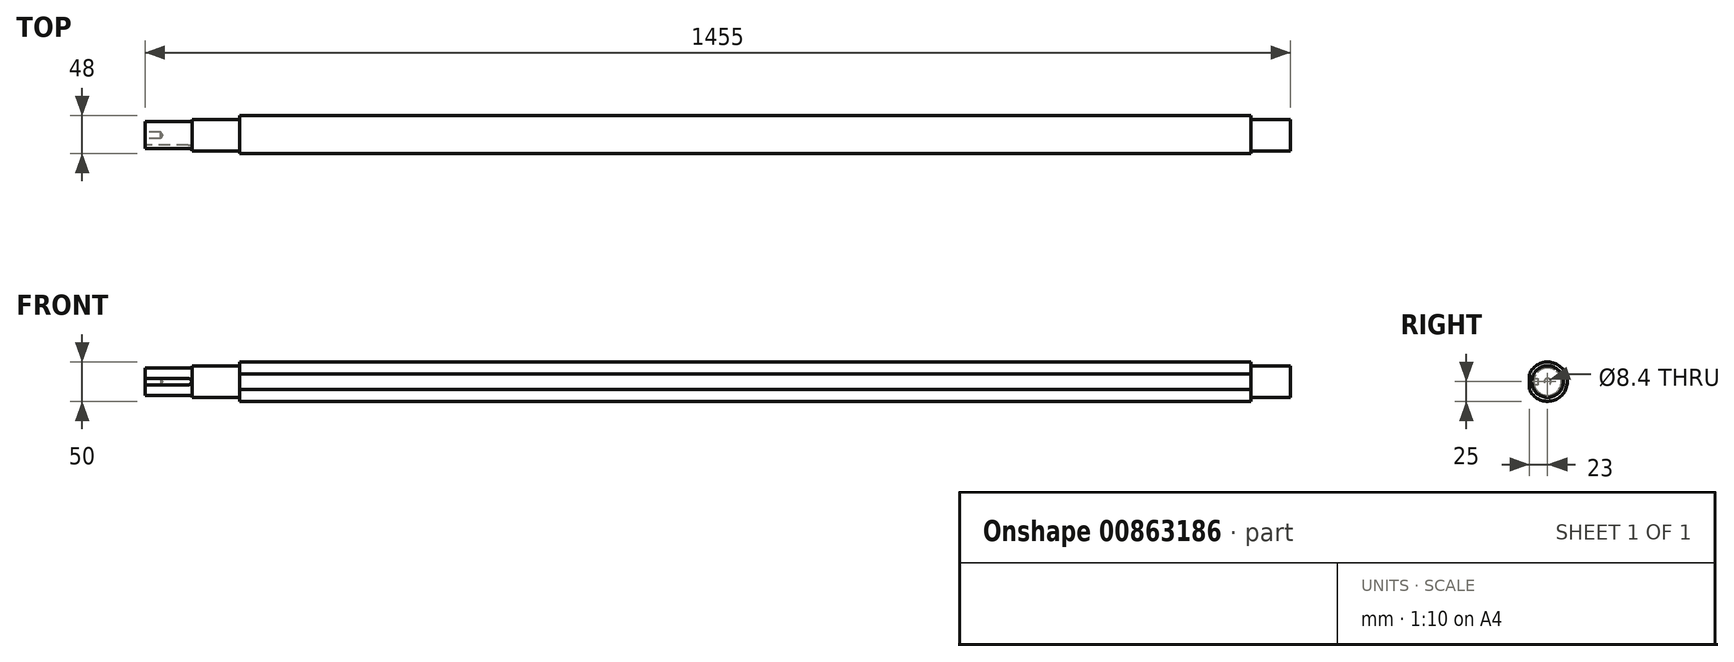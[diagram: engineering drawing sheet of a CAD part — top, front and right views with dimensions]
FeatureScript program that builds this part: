
annotation { "Feature Type Name" : "Feature", "Feature Type Description" : "" }
export const myFeature = defineFeature(function(context is Context, id is Id, definition is map)
    precondition{}
    {
        {
            var Q0;
            Q0=qCreatedBy(makeId("Front.planeOp"),FACE);
            var sketch = newSketch(context, id + "F0", { "sketchPlane" : qUnion([Q0])});
            skLineSegment(sketch, "E0", {"start": v(-727.5, 0) * mm, "end": v(727.5, 0) * mm});
            skLineSegment(sketch, "E1", {"start": v(727.5, 0) * mm, "end": v(727.5, -20) * mm});
            skLineSegment(sketch, "E2", {"start": v(727.5, -20) * mm, "end": v(677.5, -20) * mm});
            skLineSegment(sketch, "E3", {"start": v(677.5, -20) * mm, "end": v(677.5, -25) * mm});
            skLineSegment(sketch, "E4", {"start": v(677.5, -25) * mm, "end": v(-607.5, -25) * mm});
            skLineSegment(sketch, "E5", {"start": v(-607.5, -25) * mm, "end": v(-607.5, -20) * mm});
            skLineSegment(sketch, "E6", {"start": v(-607.5, -20) * mm, "end": v(-667.5, -20) * mm});
            skLineSegment(sketch, "E7", {"start": v(-727.5, -17.5) * mm, "end": v(-727.5, 0) * mm});
            skLineSegment(sketch, "E8", {"start": v(-727.5, -17.5) * mm, "end": v(-667.5, -17.5) * mm});
            skLineSegment(sketch, "E9", {"start": v(-667.5, -17.5) * mm, "end": v(-667.5, -20) * mm});
            skSolve(sketch);
        }
        {
            var Q0;
            Q0=makeQuery(id+"F0.imprint","IMPRINT",FACE,{"disambiguationData":[TD([[makeQuery(id+"F0.imprint","IMPRINT",EDGE,{"derivedFrom":sQuery(id+"F0.wireOp",EDGE,"E0")}),-1.0]])]});
            var Q1;
            Q1=sQuery(id+"F0.wireOp",EDGE,"E0");
            revolve(context, id + "F1", {"surfaceOperationType" : NewSurfaceOperationType.NEW, "entities" : qUnion([Q0]), "axis" : qUnion([Q1]), "revolveType" : RevolveType.FULL});
        }
        {
            var Q0;
            Q0=makeQuery(id+"F1.opRevolve","SWEPT_FACE",FACE,{"disambiguationData":[OSD([sQuery(id+"F0.wireOp",EDGE,"E7")])]});
            var sketch = newSketch(context, id + "F2", { "sketchPlane" : qUnion([Q0])});
            skLineSegment(sketch, "E10", {"start": v(12.5, 4) * mm, "end": v(12.5, -4) * mm});
            skLineSegment(sketch, "E11", {"start": v(12.5, -4) * mm, "end": v(17.5, -4) * mm});
            skLineSegment(sketch, "E12", {"start": v(17.5, -4) * mm, "end": v(17.5, 4) * mm});
            skLineSegment(sketch, "E13", {"start": v(17.5, 4) * mm, "end": v(12.5, 4) * mm});
            skSolve(sketch);
        }
        {
            var Q0;
            Q0=qSketchRegion(id+"F2",true);
            extrude(context, id + "F3", {"entities" : qUnion([Q0]), "operationType" : NewBodyOperationType.REMOVE, "oppositeDirection" : true, "depth" : 59 * mm, "offsetDistance" : 25 * mm});
        }
        {
            var Q0;
            Q0=makeQuery(id+"F1.opRevolve","SWEPT_FACE",FACE,{"disambiguationData":[OSD([sQuery(id+"F0.wireOp",EDGE,"E5")])]});
            var sketch = newSketch(context, id + "F4", { "sketchPlane" : qUnion([Q0])});
            skLineSegment(sketch, "E14.bottom", {"start": v(34.9, 15.3) * mm, "end": v(23, 15.3) * mm});
            skLineSegment(sketch, "E14.top", {"start": v(34.9, -18.86) * mm, "end": v(23, -18.86) * mm});
            skLineSegment(sketch, "E14.left", {"start": v(34.9, 15.3) * mm, "end": v(34.9, -18.86) * mm});
            skLineSegment(sketch, "E14.right", {"start": v(23, 15.3) * mm, "end": v(23, -18.86) * mm});
            skSolve(sketch);
        }
        {
            var Q0;
            Q0 = qSketchRegion(id + "F4", true);
            var Q1;
            Q1=makeQuery(id+"F1.opRevolve","SWEPT_FACE",FACE,{"disambiguationData":[OSD([sQuery(id+"F0.wireOp",EDGE,"E3")])]});
            extrude(context, id + "F5", {"entities" : qUnion([Q0, Q1]), "operationType" : NewBodyOperationType.REMOVE, "endBound" : BoundingType.THROUGH_ALL, "oppositeDirection" : true, "depth" : 25 * mm, "offsetDistance" : 25 * mm});
        }
        {
            var Q0;
            Q0=makeQuery(id+"F3.boolean.opBoolean","COPY",EDGE,{"derivedFrom":makeQuery(id+"F3.opExtrude","CAP_EDGE",EDGE,{"disambiguationData":[OSD([sQuery(id+"F2.wireOp",EDGE,"E13")])],"isStart":false})});
            var Q1;
            Q1=makeQuery(id+"F3.boolean.opBoolean","COPY",EDGE,{"derivedFrom":makeQuery(id+"F3.opExtrude","CAP_EDGE",EDGE,{"disambiguationData":[OSD([sQuery(id+"F2.wireOp",EDGE,"E11")])],"isStart":false})});
            fillet(context, id + "F6", {"entities" : qUnion([Q0, Q1]), "tangentPropagation" : true, "radius" : 4 * mm, "defaultsChanged" : false, "vertexSettings" : [], "allowEdgeOverflow" : false});
        }
        {
            var Q0;
            Q0=makeQuery(id+"F1.opRevolve","SWEPT_FACE",FACE,{"disambiguationData":[OSD([sQuery(id+"F0.wireOp",EDGE,"E7")])]});
            var sketch = newSketch(context, id + "F7", { "sketchPlane" : qUnion([Q0])});
            skPoint(sketch, "E15", {"position": v(0, 0) * mm});
            skSolve(sketch);
        }
        {
            var Q0;
            Q0=sQuery(id+"F7.wireOp",VERTEX,"E15");
            var Q1;
            Q1=makeQuery(id+"F1.opRevolve","SWEPT_BODY",BODY,{"disambiguationData":[OSD([sQuery(id+"F0.wireOp",EDGE,"E0"),sQuery(id+"F0.wireOp",EDGE,"E1"),sQuery(id+"F0.wireOp",EDGE,"E2"),sQuery(id+"F0.wireOp",EDGE,"E3"),sQuery(id+"F0.wireOp",EDGE,"E4"),sQuery(id+"F0.wireOp",EDGE,"E5"),sQuery(id+"F0.wireOp",EDGE,"E6"),sQuery(id+"F0.wireOp",EDGE,"E7"),sQuery(id+"F0.wireOp",EDGE,"E8"),sQuery(id+"F0.wireOp",EDGE,"E9")])]});
            hole(context, id + "F8", {"style" : HoleStyle.SIMPLE, "endStyle" : HoleEndStyle.BLIND, "standardTappedOrClearance" : lookupTablePath({ "fit" : "Close", "standard" : "ISO", "size" : "M8", "type" : "Clearance" }), "standardBlindInLast" : lookupTablePath({ "fit" : "Close", "standard" : "ISO", "engagement" : "75%", "pitch" : "1.25 mm", "size" : "M8", "type" : "Clearance & tapped" }), "holeDiameter" : 8.4 * mm, "majorDiameter" : 5 * mm, "holeDepth" : 20 * mm, "isTappedThrough" : true, "tappedDepth" : 10 * mm, "tapClearance" : 1, "startFromSketch" : true, "locations" : qUnion([Q0]), "scope" : qUnion([Q1])});
        }
    });
